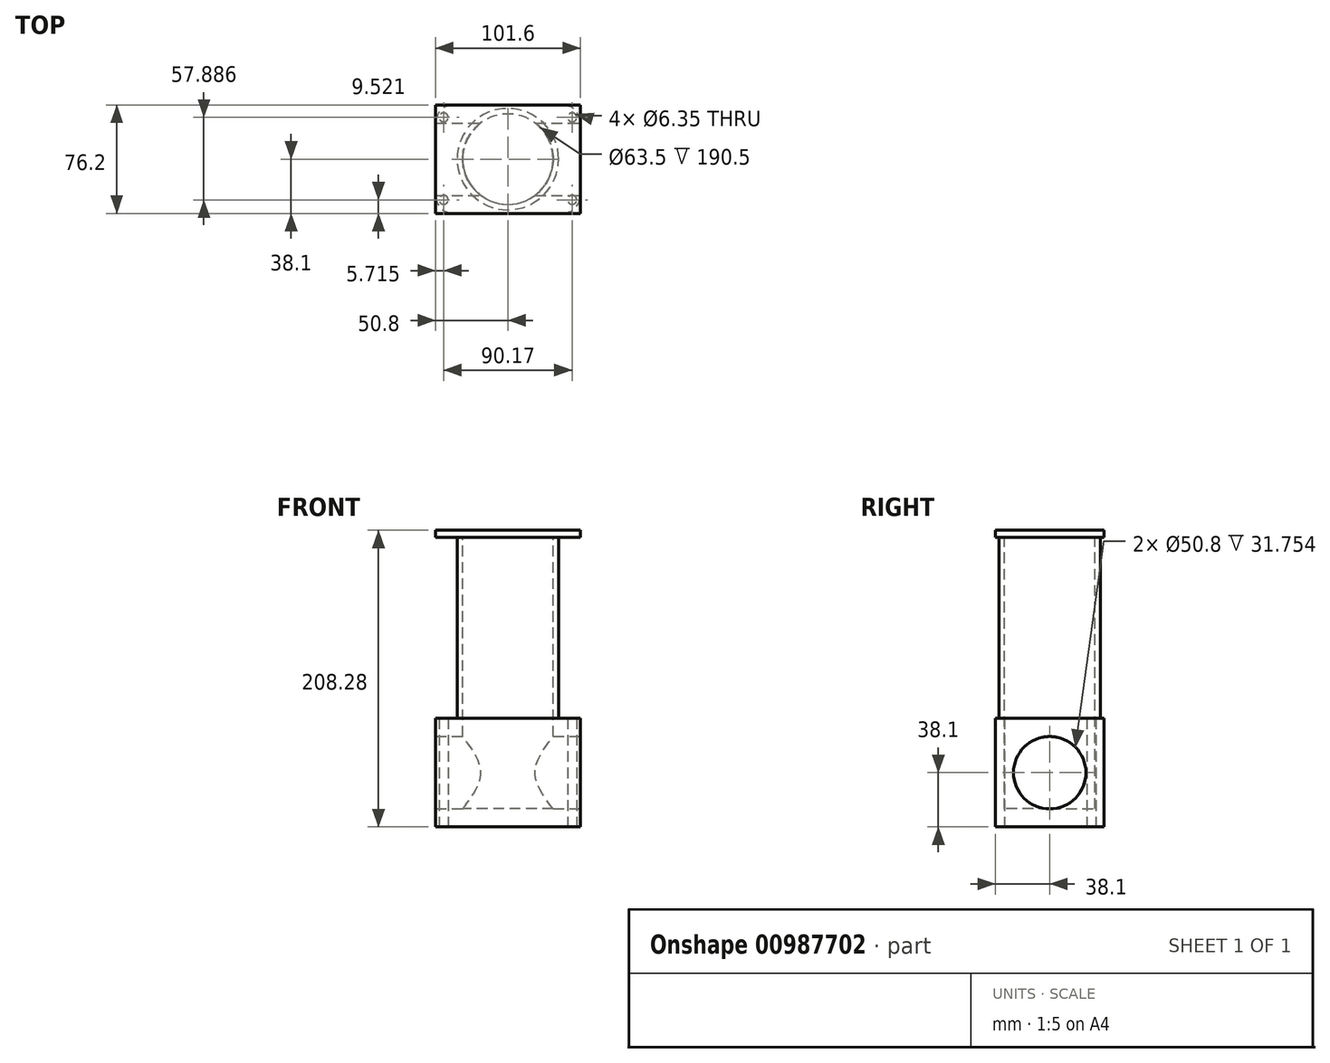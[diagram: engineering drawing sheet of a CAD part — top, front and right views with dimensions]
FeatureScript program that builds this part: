
annotation { "Feature Type Name" : "Feature", "Feature Type Description" : "" }
export const myFeature = defineFeature(function(context is Context, id is Id, definition is map)
    precondition{}
    {
        {
            var Q0;
            Q0=qCreatedBy(makeId("Top.planeOp"),FACE);
            var sketch = newSketch(context, id + "F0", { "sketchPlane" : qUnion([Q0])});
            skLineSegment(sketch, "E0.bottom", {"start": v(-50.8, 38.1) * mm, "end": v(50.8, 38.1) * mm});
            skLineSegment(sketch, "E0.top", {"start": v(-50.8, -38.1) * mm, "end": v(50.8, -38.1) * mm});
            skLineSegment(sketch, "E0.left", {"start": v(-50.8, 38.1) * mm, "end": v(-50.8, -38.1) * mm});
            skLineSegment(sketch, "E0.right", {"start": v(50.8, 38.1) * mm, "end": v(50.8, -38.1) * mm});
            skPoint(sketch, "E0.middle", {"position": v(0, 0) * mm});
            skCircle(sketch, "E1", {"center": v(45.09, -28.58) * mm, "radius": 3.18 * mm});
            skCircle(sketch, "E2", {"center": v(45.09, 29.3) * mm, "radius": 3.18 * mm});
            skCircle(sketch, "E3.MirrorC", {"center": v(-45.09, 29.3) * mm, "radius": 3.18 * mm});
            skCircle(sketch, "E4.MirrorC", {"center": v(-45.09, -28.58) * mm, "radius": 3.18 * mm});
            skSolve(sketch);
        }
        {
            var Q0;
            Q0=makeQuery(id+"F0.imprint","IMPRINT",FACE,{"disambiguationData":[TD([[makeQuery(id+"F0.imprint","IMPRINT",EDGE,{"derivedFrom":sQuery(id+"F0.wireOp",EDGE,"E0.bottom")}),-1.0]])]});
            extrude(context, id + "F1", {"entities" : qUnion([Q0]), "depth" : 203.2 * mm, "offsetDistance" : 25.4 * mm});
        }
        {
            var Q0;
            Q0=makeQuery(id+"F1.opExtrude","SWEPT_FACE",FACE,{"disambiguationData":[OSD([sQuery(id+"F0.wireOp",EDGE,"E0.right")])]});
            var sketch = newSketch(context, id + "F2", { "sketchPlane" : qUnion([Q0])});
            skCircle(sketch, "E5", {"center": v(0, 38.1) * mm, "radius": 25.4 * mm});
            skSolve(sketch);
        }
        {
            var Q0;
            Q0=makeQuery(id+"F2.imprint","IMPRINT",FACE,{"disambiguationData":[TD([[makeQuery(id+"F2.imprint","IMPRINT",EDGE,{"derivedFrom":sQuery(id+"F2.wireOp",EDGE,"E5")}),1.0]])]});
            extrude(context, id + "F3", {"entities" : qUnion([Q0]), "operationType" : NewBodyOperationType.REMOVE, "oppositeDirection" : true, "depth" : 101.6 * mm, "offsetDistance" : 25.4 * mm});
        }
        {
            var Q0;
            Q0=makeQuery(id+"F1.opExtrude","CAP_FACE",FACE,{"disambiguationData":[OSD([sQuery(id+"F0.wireOp",EDGE,"E0.bottom"),sQuery(id+"F0.wireOp",EDGE,"E0.top"),sQuery(id+"F0.wireOp",EDGE,"E0.left"),sQuery(id+"F0.wireOp",EDGE,"E0.right"),sQuery(id+"F0.wireOp",EDGE,"E1"),sQuery(id+"F0.wireOp",EDGE,"E2"),sQuery(id+"F0.wireOp",EDGE,"E3.MirrorC"),sQuery(id+"F0.wireOp",EDGE,"E4.MirrorC")])],"isStart":false});
            var sketch = newSketch(context, id + "F4", { "sketchPlane" : qUnion([Q0])});
            skLineSegment(sketch, "E6", {"start": v(0, 38.1) * mm, "end": v(0, -38.1) * mm, "construction": true});
            skLineSegment(sketch, "E7", {"start": v(-50.8, 0) * mm, "end": v(50.8, 0) * mm, "construction": true});
            skCircle(sketch, "E8", {"center": v(0, 0) * mm, "radius": 31.75 * mm});
            skSolve(sketch);
        }
        {
            var Q0;
            Q0=makeQuery(id+"F4.imprint","IMPRINT",FACE,{"disambiguationData":[TD([[makeQuery(id+"F4.imprint","IMPRINT",EDGE,{"derivedFrom":sQuery(id+"F4.wireOp",EDGE,"E8")}),1.0]])]});
            extrude(context, id + "F5", {"entities" : qUnion([Q0]), "operationType" : NewBodyOperationType.REMOVE, "oppositeDirection" : true, "depth" : 190.5 * mm, "offsetDistance" : 25.4 * mm});
        }
        {
            var Q0;
            Q0=makeQuery(id+"F1.opExtrude","SWEPT_EDGE",EDGE,{"disambiguationData":[OSD([sQuery(id+"F0.wireOp",EDGE,"E0.bottom"),sQuery(id+"F0.wireOp",EDGE,"E0.left")])]});
            var Q1;
            Q1=makeQuery(id+"F1.opExtrude","SWEPT_EDGE",EDGE,{"disambiguationData":[OSD([sQuery(id+"F0.wireOp",EDGE,"E0.top"),sQuery(id+"F0.wireOp",EDGE,"E0.left")])]});
            var Q2;
            Q2=makeQuery(id+"F1.opExtrude","SWEPT_EDGE",EDGE,{"disambiguationData":[OSD([sQuery(id+"F0.wireOp",EDGE,"E0.top"),sQuery(id+"F0.wireOp",EDGE,"E0.right")])]});
            var Q3;
            Q3=makeQuery(id+"F1.opExtrude","SWEPT_EDGE",EDGE,{"disambiguationData":[OSD([sQuery(id+"F0.wireOp",EDGE,"E0.bottom"),sQuery(id+"F0.wireOp",EDGE,"E0.right")])]});
            fillet(context, id + "F6", {"entities" : qUnion([Q0, Q1, Q2, Q3]), "radius" : 12.7 * mm, "tangentPropagation" : true, "allowEdgeOverflow" : false});
        }
        {
            var Q0;
            Q0=makeQuery(id+"F1.opExtrude","CAP_FACE",FACE,{"disambiguationData":[OSD([sQuery(id+"F0.wireOp",EDGE,"E0.bottom"),sQuery(id+"F0.wireOp",EDGE,"E0.top"),sQuery(id+"F0.wireOp",EDGE,"E0.left"),sQuery(id+"F0.wireOp",EDGE,"E0.right"),sQuery(id+"F0.wireOp",EDGE,"E1"),sQuery(id+"F0.wireOp",EDGE,"E2"),sQuery(id+"F0.wireOp",EDGE,"E3.MirrorC"),sQuery(id+"F0.wireOp",EDGE,"E4.MirrorC")])],"isStart":false});
            var sketch = newSketch(context, id + "F7", { "sketchPlane" : qUnion([Q0])});
            skCircle(sketch, "E9", {"center": v(0, 0) * mm, "radius": 35.56 * mm});
            skSolve(sketch);
        }
        {
            var Q0;
            Q0=makeQuery(id+"F7.imprint","IMPRINT",FACE,{"disambiguationData":[TD([[makeQuery(id+"F7.imprint","IMPRINT",EDGE,{"derivedFrom":sQuery(id+"F7.wireOp",EDGE,"E9")}),-1.0]])]});
            extrude(context, id + "F8", {"entities" : qUnion([Q0]), "operationType" : NewBodyOperationType.REMOVE, "oppositeDirection" : true, "depth" : 127 * mm, "offsetDistance" : 25.4 * mm});
        }
        {
            var Q0;
            Q0=qCreatedBy(makeId("Top.planeOp"),FACE);
            cPlane(context, id + "F9", {"entities" : qUnion([Q0]), "cplaneType" : CPlaneType.OFFSET, "offset" : 203.2 * mm, "width" : 152.4 * mm, "height" : 152.4 * mm});
        }
        {
            var Q0;
            Q0=qCreatedBy(id+"F9.planeOp",FACE);
            var sketch = newSketch(context, id + "F10", { "sketchPlane" : qUnion([Q0])});
            skLineSegment(sketch, "E10.bottom", {"start": v(-50.8, 38.1) * mm, "end": v(50.8, 38.1) * mm});
            skLineSegment(sketch, "E10.top", {"start": v(-50.8, -38.1) * mm, "end": v(50.8, -38.1) * mm});
            skLineSegment(sketch, "E10.left", {"start": v(-50.8, 38.1) * mm, "end": v(-50.8, -38.1) * mm});
            skLineSegment(sketch, "E10.right", {"start": v(50.8, 38.1) * mm, "end": v(50.8, -38.1) * mm});
            skPoint(sketch, "E10.middle", {"position": v(0, 0) * mm});
            skSolve(sketch);
        }
        {
            var Q0;
            Q0=makeQuery(id+"F10.imprint","IMPRINT",FACE,{"disambiguationData":[TD([[makeQuery(id+"F10.imprint","IMPRINT",EDGE,{"derivedFrom":sQuery(id+"F10.wireOp",EDGE,"E10.bottom")}),-1.0]])]});
            extrude(context, id + "F11", {"entities" : qUnion([Q0]), "operationType" : NewBodyOperationType.ADD, "depth" : 5.08 * mm, "offsetDistance" : 25.4 * mm});
        }
    });
